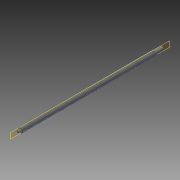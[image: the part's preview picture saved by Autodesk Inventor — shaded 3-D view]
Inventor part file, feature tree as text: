
AUTODESK INVENTOR PART (.ipt)
format: ipt  version: 2015 (Build 190159000, 159)  size: 586,752 bytes
history: native  units: mm
features: revolve x1, thread x1, chamfer x1, other x1
ambient origin geometry x8: Origin, YZ Plane, XZ Plane, XY Plane, X Axis, Y Axis, Z Axis, Center Point
bodies: Solid1 (feature_tree)
feature tree (4):
  revolve  "Revolución1"  [1 undecoded]
  thread  "Rosca1"  [1 undecoded]
  chamfer  "Chaflán1"  Distance=10.0mm
  other  "Espira1"
note: 2 required parameter values undecoded (feature->parameter linkage not recoverable at this tier; creation-order binding heuristic only, values carry confidence <= 0.55)